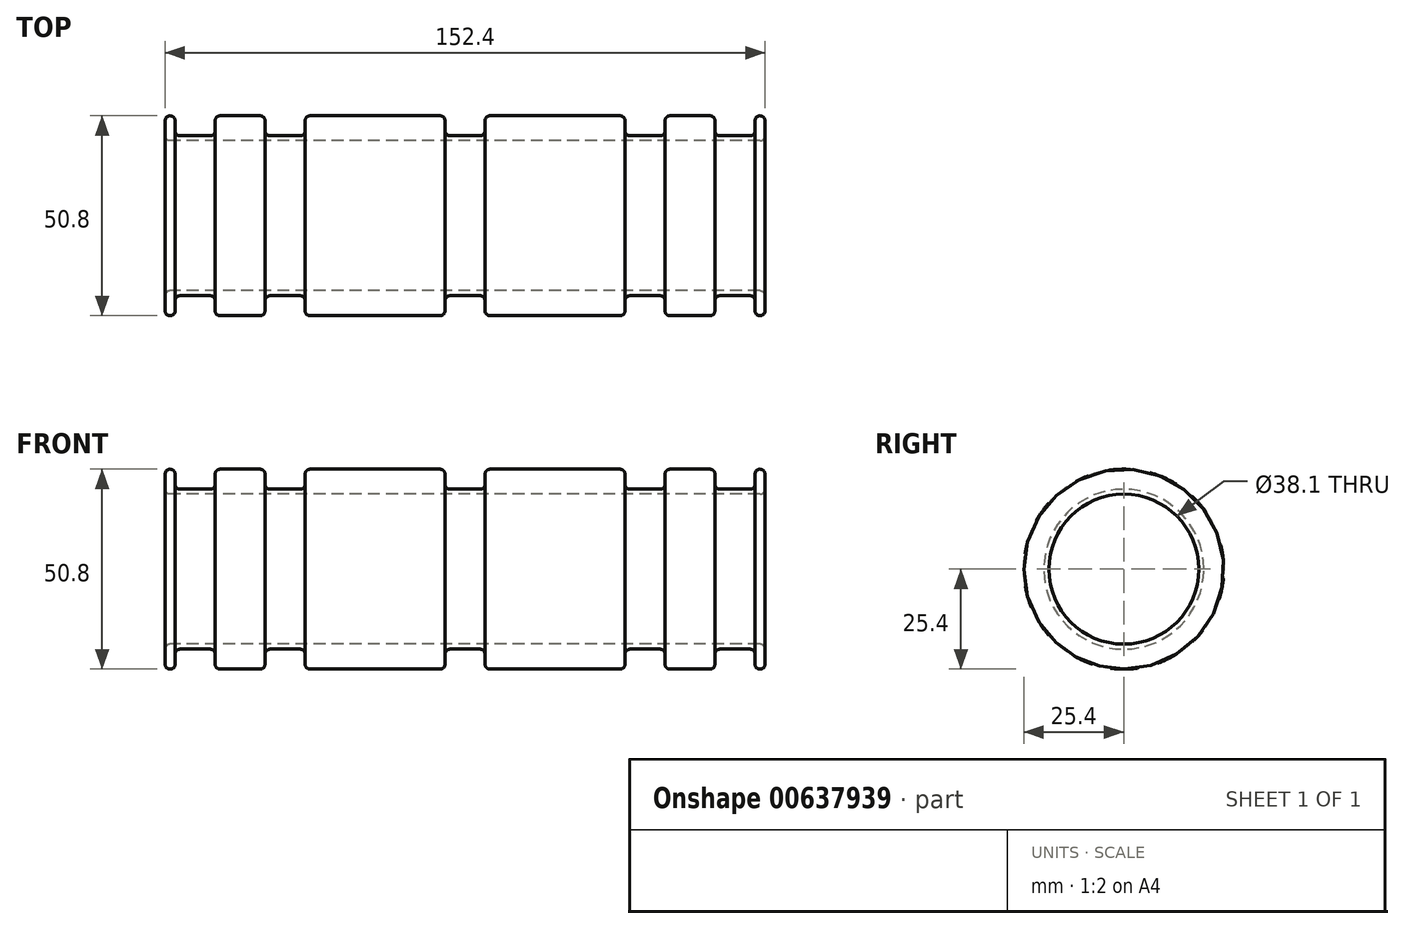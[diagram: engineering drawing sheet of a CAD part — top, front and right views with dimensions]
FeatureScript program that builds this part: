
annotation { "Feature Type Name" : "Feature", "Feature Type Description" : "" }
export const myFeature = defineFeature(function(context is Context, id is Id, definition is map)
    precondition{}
    {
        {
            var Q0;
            Q0=qCreatedBy(makeId("Right.planeOp"),FACE);
            var sketch = newSketch(context, id + "F0", { "sketchPlane" : qUnion([Q0])});
            skCircle(sketch, "E0", {"center": v(0, 0) * mm, "radius": 19.05 * mm});
            skCircle(sketch, "E1", {"center": v(0, 0) * mm, "radius": 25.4 * mm});
            skSolve(sketch);
        }
        {
            var Q0;
            Q0 = qSketchRegion(id + "F0", true);
            extrude(context, id + "F1", {"entities" : qUnion([Q0]), "endBound" : BoundingType.SYMMETRIC, "depth" : 152.4 * mm, "offsetDistance" : 25.4 * mm});
        }
        {
            var Q0;
            Q0=qCreatedBy(makeId("Front.planeOp"),FACE);
            var sketch = newSketch(context, id + "F2", { "sketchPlane" : qUnion([Q0])});
            skLineSegment(sketch, "E2.bottom", {"start": v(-63.5, 40.64) * mm, "end": v(-73.66, 40.64) * mm});
            skLineSegment(sketch, "E2.top", {"start": v(-63.5, 20.32) * mm, "end": v(-73.66, 20.32) * mm});
            skLineSegment(sketch, "E2.left", {"start": v(-63.5, 40.64) * mm, "end": v(-63.5, 20.32) * mm});
            skLineSegment(sketch, "E2.right", {"start": v(-73.66, 40.64) * mm, "end": v(-73.66, 20.32) * mm});
            skPoint(sketch, "E2.middle", {"position": v(-68.58, 30.48) * mm});
            skLineSegment(sketch, "E3.bottom", {"start": v(-40.64, 40.64) * mm, "end": v(-50.8, 40.64) * mm});
            skLineSegment(sketch, "E3.top", {"start": v(-40.64, 20.32) * mm, "end": v(-50.8, 20.32) * mm});
            skLineSegment(sketch, "E3.left", {"start": v(-40.64, 40.64) * mm, "end": v(-40.64, 20.32) * mm});
            skLineSegment(sketch, "E3.right", {"start": v(-50.8, 40.64) * mm, "end": v(-50.8, 20.32) * mm});
            skPoint(sketch, "E3.middle", {"position": v(-45.72, 30.48) * mm});
            skLineSegment(sketch, "E4.bottom", {"start": v(-17.78, 20.32) * mm, "end": v(-27.94, 20.32) * mm, "construction": true});
            skLineSegment(sketch, "E4.top", {"start": v(-17.78, 40.64) * mm, "end": v(-27.94, 40.64) * mm, "construction": true});
            skLineSegment(sketch, "E4.left", {"start": v(-17.78, 40.64) * mm, "end": v(-17.78, 20.32) * mm, "construction": true});
            skLineSegment(sketch, "E4.right", {"start": v(-27.94, 40.64) * mm, "end": v(-27.94, 20.32) * mm, "construction": true});
            skPoint(sketch, "E4.middle", {"position": v(-22.86, 30.48) * mm});
            skLineSegment(sketch, "E5", {"start": v(-63.5, 30.48) * mm, "end": v(-50.8, 30.48) * mm, "construction": true});
            skLineSegment(sketch, "E6", {"start": v(-40.64, 30.48) * mm, "end": v(-27.94, 30.48) * mm, "construction": true});
            skLineSegment(sketch, "E7.bottom", {"start": v(5.08, 40.64) * mm, "end": v(-5.08, 40.64) * mm});
            skLineSegment(sketch, "E7.top", {"start": v(5.08, 20.32) * mm, "end": v(-5.08, 20.32) * mm});
            skLineSegment(sketch, "E7.left", {"start": v(5.08, 40.64) * mm, "end": v(5.08, 20.32) * mm});
            skLineSegment(sketch, "E7.right", {"start": v(-5.08, 40.64) * mm, "end": v(-5.08, 20.32) * mm});
            skPoint(sketch, "E7.middle", {"position": v(0, 30.48) * mm});
            skPoint(sketch, "E7.middle.positionSnap0", {"position": v(-17.78, 30.48) * mm});
            skPoint(sketch, "E7.centerSnap0", {"position": v(-17.78, 30.48) * mm});
            skLineSegment(sketch, "E8.bottom", {"start": v(27.94, 40.64) * mm, "end": v(17.78, 40.64) * mm, "construction": true});
            skLineSegment(sketch, "E8.top", {"start": v(27.94, 20.32) * mm, "end": v(17.78, 20.32) * mm, "construction": true});
            skLineSegment(sketch, "E8.left", {"start": v(27.94, 40.64) * mm, "end": v(27.94, 20.32) * mm, "construction": true});
            skLineSegment(sketch, "E8.right", {"start": v(17.78, 40.64) * mm, "end": v(17.78, 20.32) * mm, "construction": true});
            skPoint(sketch, "E8.middle", {"position": v(22.86, 30.48) * mm});
            skLineSegment(sketch, "E9.bottom", {"start": v(50.8, 40.64) * mm, "end": v(40.64, 40.64) * mm});
            skLineSegment(sketch, "E9.top", {"start": v(50.8, 20.32) * mm, "end": v(40.64, 20.32) * mm});
            skLineSegment(sketch, "E9.left", {"start": v(50.8, 40.64) * mm, "end": v(50.8, 20.32) * mm});
            skLineSegment(sketch, "E9.right", {"start": v(40.64, 40.64) * mm, "end": v(40.64, 20.32) * mm});
            skPoint(sketch, "E9.middle", {"position": v(45.72, 30.48) * mm});
            skLineSegment(sketch, "E10.bottom", {"start": v(73.66, 40.64) * mm, "end": v(63.5, 40.64) * mm});
            skLineSegment(sketch, "E10.top", {"start": v(73.66, 20.32) * mm, "end": v(63.5, 20.32) * mm});
            skLineSegment(sketch, "E10.left", {"start": v(73.66, 40.64) * mm, "end": v(73.66, 20.32) * mm});
            skLineSegment(sketch, "E10.right", {"start": v(63.5, 40.64) * mm, "end": v(63.5, 20.32) * mm});
            skPoint(sketch, "E10.middle", {"position": v(68.58, 30.48) * mm});
            skLineSegment(sketch, "E11", {"start": v(-17.78, 30.48) * mm, "end": v(-5.08, 30.48) * mm, "construction": true});
            skLineSegment(sketch, "E12", {"start": v(5.08, 30.48) * mm, "end": v(17.78, 30.48) * mm, "construction": true});
            skLineSegment(sketch, "E13", {"start": v(27.94, 30.48) * mm, "end": v(40.64, 30.48) * mm, "construction": true});
            skLineSegment(sketch, "E14", {"start": v(50.8, 30.48) * mm, "end": v(63.5, 30.48) * mm, "construction": true});
            skLineSegment(sketch, "E15", {"start": v(73.66, 20.32) * mm, "end": v(76.2, 20.32) * mm, "construction": true});
            skLineSegment(sketch, "E16", {"start": v(-73.66, 20.32) * mm, "end": v(-76.2, 20.32) * mm, "construction": true});
            skSolve(sketch);
        }
        {
            var Q0;
            Q0 = qSketchRegion(id + "F2", true);
            var Q1;
            Q1=makeQuery(id+"F1.opExtrude","CAP_EDGE",EDGE,{"disambiguationData":[OSD([sQuery(id+"F0.wireOp",EDGE,"E1")])],"isStart":true});
            revolve(context, id + "F3", {"operationType" : NewBodyOperationType.REMOVE, "entities" : qUnion([Q0]), "axis" : qUnion([Q1]), "revolveType" : RevolveType.FULL, "oppositeDirection" : true});
        }
        {
            var Q0;
            {var subQ0=sQuery(id+"F0.wireOp",EDGE,"E1");Q0=makeQuery(id+"F3.boolean.opBoolean","SPLIT",FACE,{"disambiguationData":[TD([makeQuery(id+"F3.opRevolve","SWEPT_FACE",FACE,{"disambiguationData":[OSD([sQuery(id+"F2.wireOp",EDGE,"E2.right")])]})])],"derivedFrom":makeQuery(id+"F1.opExtrude","SWEPT_FACE",FACE,{"disambiguationData":[OSD([subQ0])]})});}
            var Q1;
            Q1=makeQuery(id+"F3.boolean.opBoolean","COPY",FACE,{"derivedFrom":makeQuery(id+"F3.opRevolve","SWEPT_FACE",FACE,{"disambiguationData":[OSD([sQuery(id+"F2.wireOp",EDGE,"E2.top")])]})});
            var Q2;
            Q2=makeQuery(id+"F3.boolean.opBoolean","SPLIT",FACE,{"disambiguationData":[TD([makeQuery(id+"F3.opRevolve","SWEPT_FACE",FACE,{"disambiguationData":[OSD([sQuery(id+"F2.wireOp",EDGE,"E2.left")])]})])],"derivedFrom":makeQuery(id+"F1.opExtrude","SWEPT_FACE",FACE,{"disambiguationData":[OSD([sQuery(id+"F0.wireOp",EDGE,"E1")])]})});
            var Q3;
            Q3=makeQuery(id+"F3.boolean.opBoolean","COPY",FACE,{"derivedFrom":makeQuery(id+"F3.opRevolve","SWEPT_FACE",FACE,{"disambiguationData":[OSD([sQuery(id+"F2.wireOp",EDGE,"E3.top")])]})});
            var Q4;
            Q4=makeQuery(id+"F3.boolean.opBoolean","SPLIT",FACE,{"disambiguationData":[TD([makeQuery(id+"F3.opRevolve","SWEPT_FACE",FACE,{"disambiguationData":[OSD([sQuery(id+"F2.wireOp",EDGE,"E3.left")])]})])],"derivedFrom":makeQuery(id+"F1.opExtrude","SWEPT_FACE",FACE,{"disambiguationData":[OSD([sQuery(id+"F0.wireOp",EDGE,"E1")])]})});
            var Q5;
            Q5=makeQuery(id+"F3.boolean.opBoolean","COPY",FACE,{"derivedFrom":makeQuery(id+"F3.opRevolve","SWEPT_FACE",FACE,{"disambiguationData":[OSD([sQuery(id+"F2.wireOp",EDGE,"E4.bottom")])]})});
            var Q6;
            Q6=makeQuery(id+"F3.boolean.opBoolean","SPLIT",FACE,{"disambiguationData":[TD([makeQuery(id+"F3.opRevolve","SWEPT_FACE",FACE,{"disambiguationData":[OSD([sQuery(id+"F2.wireOp",EDGE,"E4.left")])]})])],"derivedFrom":makeQuery(id+"F1.opExtrude","SWEPT_FACE",FACE,{"disambiguationData":[OSD([sQuery(id+"F0.wireOp",EDGE,"E1")])]})});
            var Q7;
            Q7=makeQuery(id+"F3.boolean.opBoolean","COPY",FACE,{"derivedFrom":makeQuery(id+"F3.opRevolve","SWEPT_FACE",FACE,{"disambiguationData":[OSD([sQuery(id+"F2.wireOp",EDGE,"E7.top")])]})});
            var Q8;
            Q8=makeQuery(id+"F3.boolean.opBoolean","SPLIT",FACE,{"disambiguationData":[TD([makeQuery(id+"F3.opRevolve","SWEPT_FACE",FACE,{"disambiguationData":[OSD([sQuery(id+"F2.wireOp",EDGE,"E7.left")])]})])],"derivedFrom":makeQuery(id+"F1.opExtrude","SWEPT_FACE",FACE,{"disambiguationData":[OSD([sQuery(id+"F0.wireOp",EDGE,"E1")])]})});
            var Q9;
            Q9=makeQuery(id+"F3.boolean.opBoolean","COPY",FACE,{"derivedFrom":makeQuery(id+"F3.opRevolve","SWEPT_FACE",FACE,{"disambiguationData":[OSD([sQuery(id+"F2.wireOp",EDGE,"E8.top")])]})});
            var Q10;
            Q10=makeQuery(id+"F3.boolean.opBoolean","SPLIT",FACE,{"disambiguationData":[TD([makeQuery(id+"F3.opRevolve","SWEPT_FACE",FACE,{"disambiguationData":[OSD([sQuery(id+"F2.wireOp",EDGE,"E8.left")])]})])],"derivedFrom":makeQuery(id+"F1.opExtrude","SWEPT_FACE",FACE,{"disambiguationData":[OSD([sQuery(id+"F0.wireOp",EDGE,"E1")])]})});
            var Q11;
            Q11=makeQuery(id+"F3.boolean.opBoolean","COPY",FACE,{"derivedFrom":makeQuery(id+"F3.opRevolve","SWEPT_FACE",FACE,{"disambiguationData":[OSD([sQuery(id+"F2.wireOp",EDGE,"E9.top")])]})});
            var Q12;
            Q12=makeQuery(id+"F3.boolean.opBoolean","SPLIT",FACE,{"disambiguationData":[TD([makeQuery(id+"F3.opRevolve","SWEPT_FACE",FACE,{"disambiguationData":[OSD([sQuery(id+"F2.wireOp",EDGE,"E9.left")])]})])],"derivedFrom":makeQuery(id+"F1.opExtrude","SWEPT_FACE",FACE,{"disambiguationData":[OSD([sQuery(id+"F0.wireOp",EDGE,"E1")])]})});
            var Q13;
            Q13=makeQuery(id+"F3.boolean.opBoolean","COPY",FACE,{"derivedFrom":makeQuery(id+"F3.opRevolve","SWEPT_FACE",FACE,{"disambiguationData":[OSD([sQuery(id+"F2.wireOp",EDGE,"E10.top")])]})});
            var Q14;
            {var subQ0=sQuery(id+"F0.wireOp",EDGE,"E1");Q14=makeQuery(id+"F3.boolean.opBoolean","SPLIT",FACE,{"disambiguationData":[TD([makeQuery(id+"F3.opRevolve","SWEPT_FACE",FACE,{"disambiguationData":[OSD([sQuery(id+"F2.wireOp",EDGE,"E10.left")])]})])],"derivedFrom":makeQuery(id+"F1.opExtrude","SWEPT_FACE",FACE,{"disambiguationData":[OSD([subQ0])]})});}
            var Q15;
            Q15=makeQuery(id+"F1.opExtrude","CAP_EDGE",EDGE,{"disambiguationData":[OSD([sQuery(id+"F0.wireOp",EDGE,"E0")])],"isStart":true});
            var Q16;
            Q16=makeQuery(id+"F1.opExtrude","CAP_EDGE",EDGE,{"disambiguationData":[OSD([sQuery(id+"F0.wireOp",EDGE,"E0")])],"isStart":false});
            fillet(context, id + "F4", {"entities" : qUnion([Q0, Q1, Q2, Q3, Q4, Q5, Q6, Q7, Q8, Q9, Q10, Q11, Q12, Q13, Q14, Q15, Q16]), "radius" : 1.27 * mm, "tangentPropagation" : true, "allowEdgeOverflow" : false});
        }
    });
